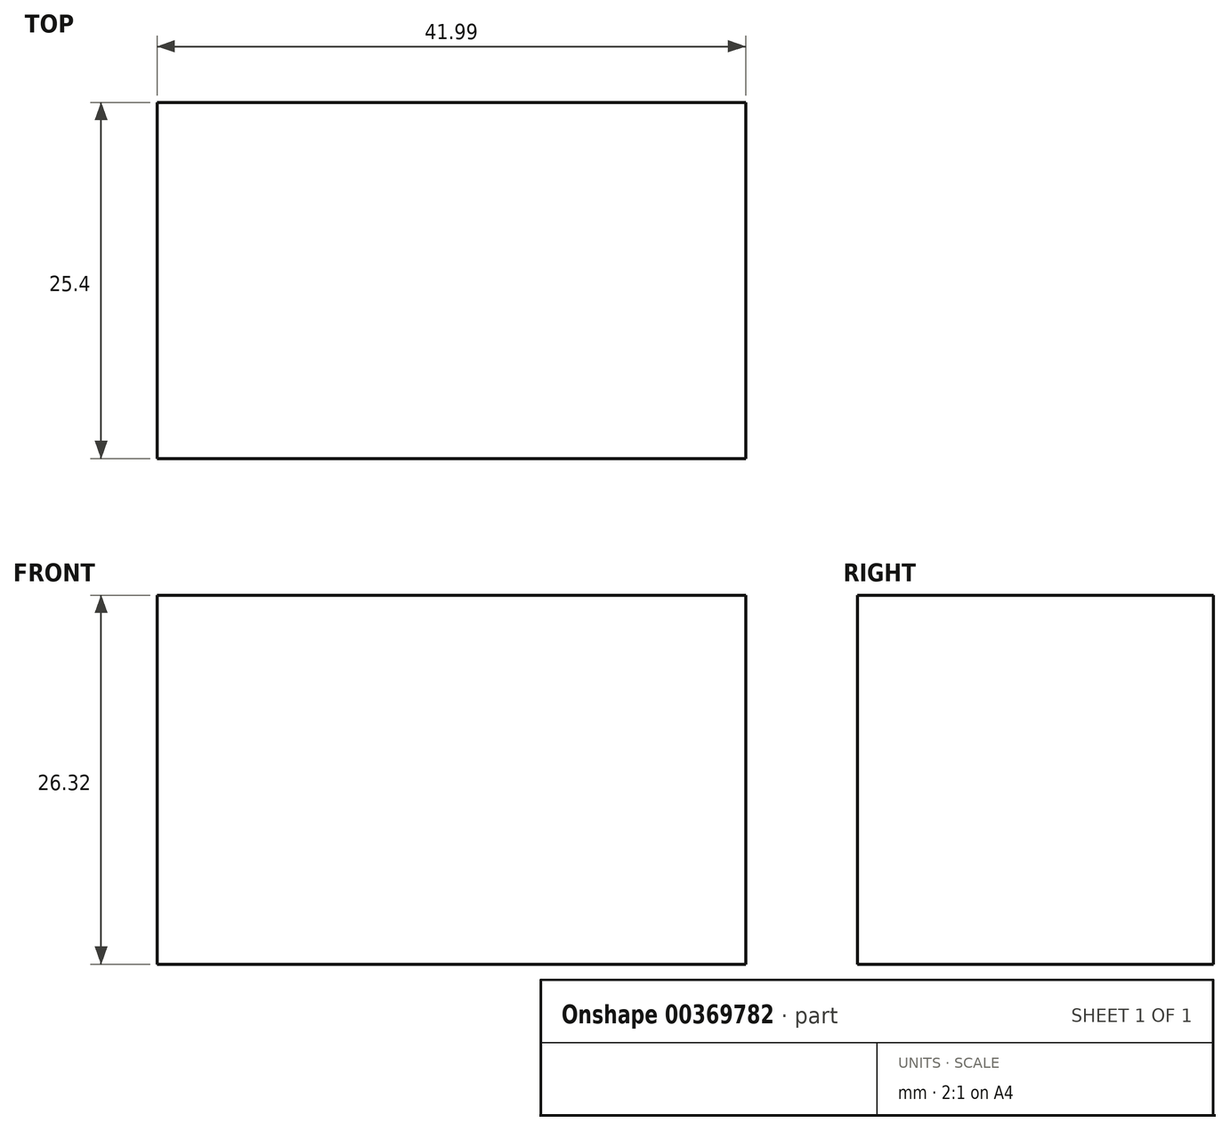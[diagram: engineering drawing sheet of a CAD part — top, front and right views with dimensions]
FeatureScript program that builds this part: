
annotation { "Feature Type Name" : "Feature", "Feature Type Description" : "" }
export const myFeature = defineFeature(function(context is Context, id is Id, definition is map)
    precondition{}
    {
        {
            var Q0;
            Q0=qCreatedBy(makeId("Front.planeOp"),FACE);
            var sketch = newSketch(context, id + "F0", { "sketchPlane" : qUnion([Q0])});
            skLineSegment(sketch, "E0.bottom", {"start": v(-16.76, 26.32) * mm, "end": v(25.23, 26.32) * mm});
            skLineSegment(sketch, "E0.top", {"start": v(-16.76, 0) * mm, "end": v(25.23, 0) * mm});
            skLineSegment(sketch, "E0.left", {"start": v(-16.76, 26.32) * mm, "end": v(-16.76, 0) * mm});
            skLineSegment(sketch, "E0.right", {"start": v(25.23, 26.32) * mm, "end": v(25.23, 0) * mm});
            skSolve(sketch);
        }
        {
            var Q0;
            Q0 = qSketchRegion(id + "F0", true);
            extrude(context, id + "F1", {"entities" : qUnion([Q0]), "depth" : 25.4 * mm});
        }
    });
